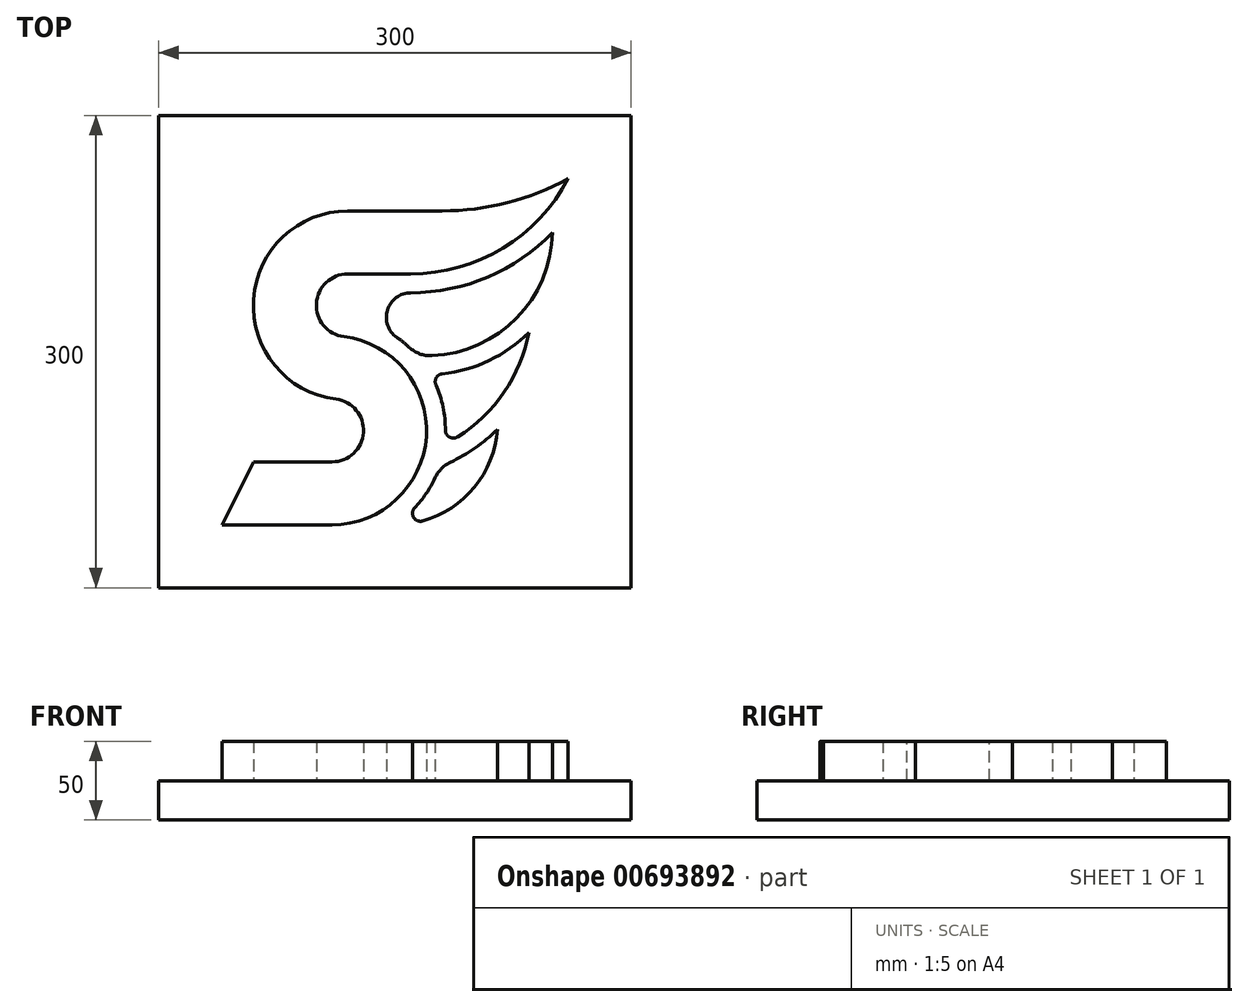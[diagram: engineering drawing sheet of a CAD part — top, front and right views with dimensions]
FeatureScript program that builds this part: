
annotation { "Feature Type Name" : "Feature", "Feature Type Description" : "" }
export const myFeature = defineFeature(function(context is Context, id is Id, definition is map)
    precondition{}
    {
        {
            var Q0;
            Q0=qCreatedBy(makeId("Top.planeOp"),FACE);
            var sketch = newSketch(context, id + "F0", { "sketchPlane" : qUnion([Q0])});
            skLineSegment(sketch, "E0.bottom", {"start": v(150, 150) * mm, "end": v(-150, 150) * mm});
            skLineSegment(sketch, "E0.top", {"start": v(150, -150) * mm, "end": v(-150, -150) * mm});
            skLineSegment(sketch, "E0.left", {"start": v(150, 150) * mm, "end": v(150, -150) * mm});
            skLineSegment(sketch, "E0.right", {"start": v(-150, 150) * mm, "end": v(-150, -150) * mm});
            skPoint(sketch, "E0.middle", {"position": v(0, 0) * mm});
            skSolve(sketch);
        }
        {
            var Q0;
            Q0=makeQuery(id+"F0.imprint","IMPRINT",FACE,{"disambiguationData":[TD([[makeQuery(id+"F0.imprint","IMPRINT",EDGE,{"derivedFrom":sQuery(id+"F0.wireOp",EDGE,"E0.bottom")}),1.0]])]});
            extrude(context, id + "F1", {"entities" : qUnion([Q0]), "oppositeDirection" : true, "depth" : 25 * mm, "offsetDistance" : 25 * mm});
        }
        {
            var Q0;
            Q0=makeQuery(id+"F1.opExtrude","CAP_FACE",FACE,{"disambiguationData":[OSD([sQuery(id+"F0.wireOp",EDGE,"E0.bottom"),sQuery(id+"F0.wireOp",EDGE,"E0.top"),sQuery(id+"F0.wireOp",EDGE,"E0.left"),sQuery(id+"F0.wireOp",EDGE,"E0.right")])],"isStart":true});
            var sketch = newSketch(context, id + "F2", { "sketchPlane" : qUnion([Q0])});
            skArc(sketch, "E1", {"start": v(-40, -70) * mm, "mid": v(-20.04, -51.25) * mm, "end": v(-37.5, -30.16) * mm});
            skArc(sketch, "E2", {"start": v(-40, -110) * mm, "mid": v(19.88, -53.76) * mm, "end": v(-32.5, 9.53) * mm});
            skArc(sketch, "E3", {"start": v(-30, 49.37) * mm, "mid": v(-49.96, 30.62) * mm, "end": v(-32.5, 9.53) * mm});
            skArc(sketch, "E4", {"start": v(-30, 89.37) * mm, "mid": v(-89.88, 33.13) * mm, "end": v(-37.5, -30.16) * mm});
            skLineSegment(sketch, "E5.bottom", {"start": v(-40, -70) * mm, "end": v(-90, -70) * mm});
            skLineSegment(sketch, "E5.top", {"start": v(-40, -110) * mm, "end": v(-110, -110) * mm});
            skLineSegment(sketch, "E6", {"start": v(-110, -110) * mm, "end": v(-90, -70) * mm});
            skLineSegment(sketch, "E7.bottom", {"start": v(-30, 49.37) * mm, "end": v(10, 49.37) * mm});
            skLineSegment(sketch, "E7.top", {"start": v(-30, 89.37) * mm, "end": v(30, 89.37) * mm});
            skArc(sketch, "E8", {"start": v(30, 89.37) * mm, "mid": v(71.3, 94.61) * mm, "end": v(110, 110) * mm});
            skArc(sketch, "E9", {"start": v(10, 49.37) * mm, "mid": v(68.47, 65.71) * mm, "end": v(110, 110) * mm});
            skArc(sketch, "E10", {"start": v(-0.2, -110) * mm, "mid": v(16.97, -94.03) * mm, "end": v(28.1, -73.4) * mm});
            skArc(sketch, "E11", {"start": v(10, 37.37) * mm, "mid": v(58.91, 47.36) * mm, "end": v(100, 75.72) * mm});
            skArc(sketch, "E12", {"start": v(10, 37.37) * mm, "mid": v(-4.82, 26.5) * mm, "end": v(1.13, 9.1) * mm});
            skArc(sketch, "E13", {"start": v(14.04, -2.42) * mm, "mid": v(73.83, 18.16) * mm, "end": v(100, 75.72) * mm});
            skLineSegment(sketch, "E14", {"start": v(10, 37.37) * mm, "end": v(14.04, -2.42) * mm, "construction": true});
            skArc(sketch, "E15", {"start": v(22.7, -14.6) * mm, "mid": v(56.41, -7.14) * mm, "end": v(85, 12.23) * mm});
            skArc(sketch, "E16", {"start": v(31.47, -58.75) * mm, "mid": v(66.55, -29.53) * mm, "end": v(85, 12.23) * mm});
            skLineSegment(sketch, "E17", {"start": v(22.7, -14.6) * mm, "end": v(31.47, -58.75) * mm, "construction": true});
            skArc(sketch, "E18", {"start": v(28.1, -73.4) * mm, "mid": v(47.74, -63.24) * mm, "end": v(65, -49.42) * mm});
            skArc(sketch, "E19", {"start": v(-0.2, -110) * mm, "mid": v(44.3, -92.52) * mm, "end": v(65, -49.42) * mm});
            skArc(sketch, "E20.trimOffspring", {"start": v(14.04, -2.42) * mm, "mid": v(7.93, 3.73) * mm, "end": v(1.13, 9.1) * mm});
            skArc(sketch, "E21.trimOffspring", {"start": v(31.47, -58.75) * mm, "mid": v(30.62, -35.97) * mm, "end": v(22.7, -14.6) * mm});
            skArc(sketch, "E22", {"start": v(-229.44, -50.42) * mm, "mid": v(-169.02, -110) * mm, "end": v(-109.44, -49.58) * mm});
            skArc(sketch, "E23", {"start": v(-145, 29.8) * mm, "mid": v(-170.3, 54.37) * mm, "end": v(-195, 29.2) * mm});
            skArc(sketch, "E24", {"start": v(-194.44, -50.18) * mm, "mid": v(-169.35, -75) * mm, "end": v(-144.44, -50) * mm});
            skLineSegment(sketch, "E25", {"start": v(-230, 28.95) * mm, "end": v(-229.44, -50.42) * mm});
            skLineSegment(sketch, "E26.trimOffspring", {"start": v(-109.44, -49.58) * mm, "end": v(-109.72, -10) * mm});
            skArc(sketch, "E27.trimOffspring", {"start": v(-110, 29.8) * mm, "mid": v(-170.42, 89.37) * mm, "end": v(-230, 28.95) * mm});
            skLineSegment(sketch, "E28", {"start": v(-195, 29.2) * mm, "end": v(-194.44, -50.18) * mm});
            skLineSegment(sketch, "E29", {"start": v(-110, 29.8) * mm, "end": v(-145, 29.8) * mm});
            skLineSegment(sketch, "E30", {"start": v(-109.72, -10) * mm, "end": v(-154.44, -10) * mm});
            skLineSegment(sketch, "E31", {"start": v(-154.44, -10) * mm, "end": v(-154.44, -40) * mm});
            skLineSegment(sketch, "E32", {"start": v(-154.44, -40) * mm, "end": v(-144.44, -40) * mm});
            skLineSegment(sketch, "E33", {"start": v(-144.44, -40) * mm, "end": v(-144.44, -50) * mm});
            skSolve(sketch);
        }
        {
            var Q0;
            Q0=makeQuery(id+"F2.imprint","IMPRINT",FACE,{"disambiguationData":[TD([[makeQuery(id+"F2.imprint","IMPRINT",EDGE,{"derivedFrom":sQuery(id+"F2.wireOp",EDGE,"E1")}),-1.0]])]});
            var Q1;
            Q1=makeQuery(id+"F2.imprint","IMPRINT",FACE,{"disambiguationData":[TD([[makeQuery(id+"F2.imprint","IMPRINT",EDGE,{"derivedFrom":sQuery(id+"F2.wireOp",EDGE,"E11")}),-1.0]])]});
            var Q2;
            Q2=makeQuery(id+"F2.imprint","IMPRINT",FACE,{"disambiguationData":[TD([[makeQuery(id+"F2.imprint","IMPRINT",EDGE,{"derivedFrom":sQuery(id+"F2.wireOp",EDGE,"E15")}),-1.0]])]});
            var Q3;
            Q3=makeQuery(id+"F2.imprint","IMPRINT",FACE,{"disambiguationData":[TD([[makeQuery(id+"F2.imprint","IMPRINT",EDGE,{"derivedFrom":sQuery(id+"F2.wireOp",EDGE,"E10")}),-1.0]])]});
            extrude(context, id + "F3", {"entities" : qUnion([Q0, Q1, Q2, Q3]), "operationType" : NewBodyOperationType.ADD, "depth" : 25 * mm, "offsetDistance" : 25 * mm});
        }
        {
            var Q0;
            Q0=makeQuery(id+"F3.opExtrude","SWEPT_EDGE",EDGE,{"disambiguationData":[OSD([sQuery(id+"F2.wireOp",EDGE,"E13"),sQuery(id+"F2.wireOp",EDGE,"E20.trimOffspring")])]});
            var Q1;
            Q1=makeQuery(id+"F3.opExtrude","SWEPT_EDGE",EDGE,{"disambiguationData":[OSD([sQuery(id+"F2.wireOp",EDGE,"E10"),sQuery(id+"F2.wireOp",EDGE,"E18")])]});
            fillet(context, id + "F4", {"entities" : qUnion([Q0, Q1]), "radius" : 20 * mm, "tangentPropagation" : true, "allowEdgeOverflow" : false});
        }
        {
            var Q0;
            Q0=makeQuery(id+"F3.opExtrude","SWEPT_EDGE",EDGE,{"disambiguationData":[OSD([sQuery(id+"F2.wireOp",EDGE,"E15"),sQuery(id+"F2.wireOp",EDGE,"E21.trimOffspring")])]});
            var Q1;
            Q1=makeQuery(id+"F3.opExtrude","SWEPT_EDGE",EDGE,{"disambiguationData":[OSD([sQuery(id+"F2.wireOp",EDGE,"E16"),sQuery(id+"F2.wireOp",EDGE,"E21.trimOffspring")])]});
            var Q2;
            Q2=makeQuery(id+"F3.opExtrude","SWEPT_EDGE",EDGE,{"disambiguationData":[OSD([sQuery(id+"F2.wireOp",EDGE,"E10"),sQuery(id+"F2.wireOp",EDGE,"E19")])]});
            fillet(context, id + "F5", {"entities" : qUnion([Q0, Q1, Q2]), "radius" : 5 * mm, "tangentPropagation" : true, "allowEdgeOverflow" : false});
        }
    });
